# Revit family: PRE080019-FR
name_source: partatom
category: Appareils sanitaires
revit_build: Autodesk Revit 2017 (Build: 20160225_1515(x64)
units: mm (PartAtom-declared; Revit-internal decimal feet)

## family parameters
Basée sur le plan de construction = Non
Cote de connecteur circulaire = Utiliser le diamètre
Couper avec des vides une fois chargée = Non
Partagée = Non
Point de calcul de pièce = Non
Toujours verticalement = Oui
Type d'élément = Normal

## types (1)
- 70814 PRESTO CHEF Colonne deux trous murale avec douchette
    Adresse = 7, RUE RACINE - 92542 MONTROUGE CEDEX FRANCE
    Debit = 3 l/min par limiteur de débit intégré

Aérateur anti-tartre haute qualité

Dispositif anti-coup de bélier
    Description = Produit résistant à un usage intensif
Souplesse du ressort
Douchette ergonomique avec fonction écoulement continu, et surface de préhension limitant les risques de brûlure. Embout permettant d'absorber les chocs. Crochet
de blocage pour éviter les TMS ( troubles musculo squelettiques)
Interface corps/colonne renforcé
Volants intuitifs et ergonomiques : facilité de préhension
Version murale : facilite le nettoyage et favorise une hygiène optimale
Support mural réglable
Flexible de douchette gaine PVC pour éviter les niches bactériennes et faciliter le nettoyage
Maintenance aisée : présence d'une fente sous la pastille rouge/ bleue permettant le passage d'un tournevis
Facilité de maintenance : disponibilité de toutes les pièces d'usure
    Diamètre Nominal = 15 mm  [stored 0.0492126 ft]
    Edition number = 0
    Fabricant = LES ROBINETS PRESTO S.A.
    Finition = Corps en laiton chromé conforme aux normes NF EN1982/ NF EN 12164 / NF EN 12165
Traitement de surface Nickel-Chrome selon NF EN12540
Résistance au brouillard salin neutre (NSS) : 200 h selon NF ISO 9233
    Flux = 0.1 L/s
    Fonction = Mélangeur à tête céramique 1/4 de tour
Douchette noire M1/2'' avec surface de préhension limitant les risques de brûlure
Débit de douchette régulé à 12L/min. Jet réglable par l'utilisateur : concentré ou mouillage. Embout de douchette anti-tartre. Crochet de blocage pour écoulement
continu. Clapet anti-retour intégré.
Ressort de guidage pour flexible en inox
Support mural réglable, recoupable de 60 à 200 mm (de la colonne au mur)
Support de douchette ajustable : à gauche ou à droite

Pression d'utilisation recommandée : 1 à 5 bars

Débit de douchette : 12L/min à 3 bar

Alimentation hydraulique : G 1/2'' (15x 21)

Matière et couleur de finition :
Corps et colonne en laiton chromé
Matière conforme avec la liste "UBA"

Résistance thermique : Résiste à une température de 75° C durant 30 minutes (dans le cadre de chocs thermiques).

Livré avec :
Rosaces excentriques
2 filtres
1 flexible (de douchette) tressé inox entouré d'une gaine PVC, résistant à des températures allant jusqu'à 90°C. Température d'utilisation en service à 70°C maximum
en continu
    HC = 1100 mm
    Hauteur = 1134 mm  [stored 3.72047 ft]
    Largeur = 217 mm  [stored 0.711942 ft]
    Lien CCTP = http://www.prestodatashare.com
    Lien fiche produit = http://www.prestodatashare.com
    Lien notice d'utilisation = http://www.prestodatashare.com
    Matériau = Laiton poli chromé
    Modèle = 70814 PRESTO CHEF Colonne deux trous murale avec douchette
    Perte de charge = 0.0 Pa
    Polantis code = PRE080019
    Pression = 1 à 5 bars
    Product Guid = f28a7723-6234-452e-aff1-106aed1f1b57
    Product data url = https://www.bimobject.com
    Profondeur = 300 mm  [stored 0.984252 ft]
    Raccordement = 2xG1/2 entraxe 150 derriere bas
    Reference = 70814
    URL = http://www.prestodatashare.com
    URL Fabricant = http://www.prestodatashare.com
    Variantes = 70814

note: [stored X ft] marks values corroborated as IEEE doubles in the binary element streams (Revit-internal decimal feet)
